# Revit family: GU2013002
name_source: partatom
category: Plumbing Fixtures
revit_build: Autodesk Revit 2016 (Build: 20150220_1215(x64)
units: mm (PartAtom-declared; Revit-internal decimal feet)

## family parameters
Always vertical = Yes
Cut with Voids When Loaded = No
Host = Wall
OmniClass Number = 23.45.00.00
OmniClass Title = Sanitary, Laundry, and Cleaning Equipment
Part Type = Normal
Room Calculation Point = No
Round Connector Dimension = Use Diameter
Shared = No

## types (1)
- 370 x 310
    Assembly Code = D2010
    CW Connection = Yes
    Description = Urinario suspendido de porcelana vitrificada
Planos con alimentacion superior, rociador
perimetral y sifón incorporado. Urinario de alta eficiencia
Alimentacion universal de 5.5 cm dl muro
Descarga horizontal al muro.
    HW Connection = No
    Manufacturer = CHC
    Material = Porcelain, Linen
    Model = GU2013002
    Type Image = GU2013002.jpg
    URL = www.grupochc.cl
    Vent Connection = No
    Waste Connection = No

## geometry (parser evidence)
native form markers: Sweep x2
no freeform markers — native parametric forms only
